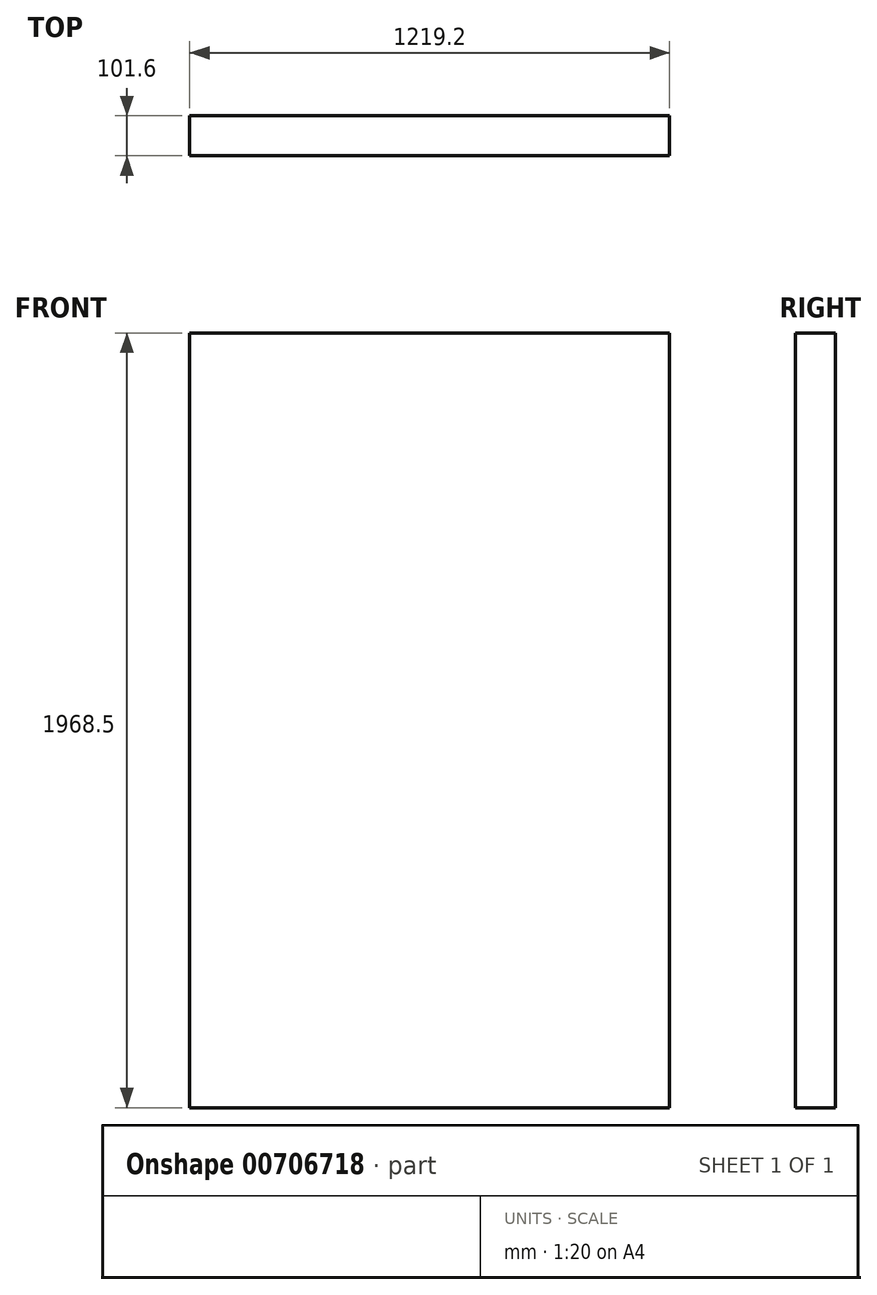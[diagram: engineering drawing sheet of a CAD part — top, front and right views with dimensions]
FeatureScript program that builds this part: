
annotation { "Feature Type Name" : "Feature", "Feature Type Description" : "" }
export const myFeature = defineFeature(function(context is Context, id is Id, definition is map)
    precondition{}
    {
        {
            var Q0;
            Q0=qCreatedBy(makeId("Front.planeOp"),FACE);
            var sketch = newSketch(context, id + "F0", { "sketchPlane" : qUnion([Q0])});
            skLineSegment(sketch, "E0.bottom", {"start": v(0, 0) * mm, "end": v(1219.2, 0) * mm});
            skLineSegment(sketch, "E0.top", {"start": v(0, 1968.5) * mm, "end": v(1219.2, 1968.5) * mm});
            skLineSegment(sketch, "E0.left", {"start": v(0, 0) * mm, "end": v(0, 1968.5) * mm});
            skLineSegment(sketch, "E0.right", {"start": v(1219.2, 0) * mm, "end": v(1219.2, 1968.5) * mm});
            skSolve(sketch);
        }
        {
            var Q0;
            Q0=makeQuery(id+"F0.imprint","IMPRINT",FACE,{"disambiguationData":[TD([[makeQuery(id+"F0.imprint","IMPRINT",EDGE,{"derivedFrom":sQuery(id+"F0.wireOp",EDGE,"E0.bottom")}),1.0]])]});
            extrude(context, id + "F1", {"entities" : qUnion([Q0]), "depth" : 101.6 * mm, "offsetDistance" : 25.4 * mm});
        }
    });
